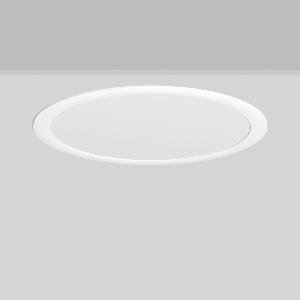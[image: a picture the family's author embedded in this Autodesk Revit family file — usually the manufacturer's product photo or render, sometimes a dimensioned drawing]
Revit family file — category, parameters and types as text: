
# Revit family: toledo_flat_round_e_672385_002_1_07_27f4
name_source: partatom
category: Lighting Fixtures
units: mm (PartAtom-declared; Revit-internal decimal feet)

## family parameters
Cut with Voids When Loaded = No
Host = Face
Light Source = No
Part Type = Normal
Room Calculation Point = No
Round Connector Dimension = Use Diameter
Shared = No

## types (1)
- TOLEDO FLAT round E (1 x LED Modul 840, 3600 lm, 4000)
    Apparent Load = 30 VA
    CIE Flux Codes = 48 79 96 100 100
    Color Rendering = 80
    Color Temperature = 4000
    Default Elevation = 1800 mm
    Description = Series: TOLEDO FLAT round
Ultra thin recessed downlight. For escape route illumination. Housing: die-cast aluminium, powder-coated. Ceiling installation with spring system. Including separate LED converter with connecting cable 250 mm. Self-contained system with automatic self-test and feedback via DALI bus, only to RZB DALI monitoring system. External driver with simple plug-in locking system. 
Colour: white
Diameter: 495 mm
Height: 6 mm
Cut-out diameter: 470 mm
Recess height: 70 mm
Luminaire: recess height: 60-80 mm
Weight: 3.38 kg
Operating mode: maintained power mode
Duration time: 8 h
Lamp: LED
Socket: without socket
Colour temperature: 4000K
Colour rendering index (CRI): 80
System power: 30 W
Rated luminous flux: 3600 lm
Luminous flux, emergency: 170 lm
System power, emergency: -
Control gear: Regulated power supply
Protection class: I
Type of protection: IP 54
    Height = 0 mm  [stored 0 ft]
    Lamp = 1 x LED Modul 840
    Lamp Light Flux = 3600 lm
    Lamp count = 1
    Length = 495 mm
    Lifetime = 50000 h
    Luminous efficacy = 120 lm/W
    Manufacturer = RZB
    ModVariant = No
    Model = 672385.002.1.07
    Mounting Place = Ceiling
    Mounting Type = Recessed
    Number of Poles = 1
    OnlyDefault = Yes
    Power Factor = 1
    Product Name = TOLEDO FLAT round E
    Product group = Recessed downlights
    ProductGroupID = 402
    Protection Class = Protection class I
    Protection Degree = IP 40
    RLX_Detail_Level = 1
    RLX_Emergency_Light_Flux = 170 lm
    RLX_Emergency_Type = 3
    RLX_Emergency_Type_DB = Yes
    RlxData = <blob elided: 35193 chars, md5=573b3030>
    Socket = socket
    Standby Power = 0 W
    System Light Flux = 3600 lm
    System Power = 30 W
    Type Comments = Product without accessories
    Type Image = 901585.002.jpg
    URL = http://relux.com
    VarID = ---
    Voltage = 230 V
    Voltage Range = 220-240 V
    Weight = 0.00 kg
    Width = 0 mm  [stored 0 ft]

note: [stored X ft] marks values corroborated as IEEE doubles in the binary element streams (Revit-internal decimal feet)

## geometry (parser evidence)
native form markers: Blend x4, Sweep x11
no freeform markers — native parametric forms only
